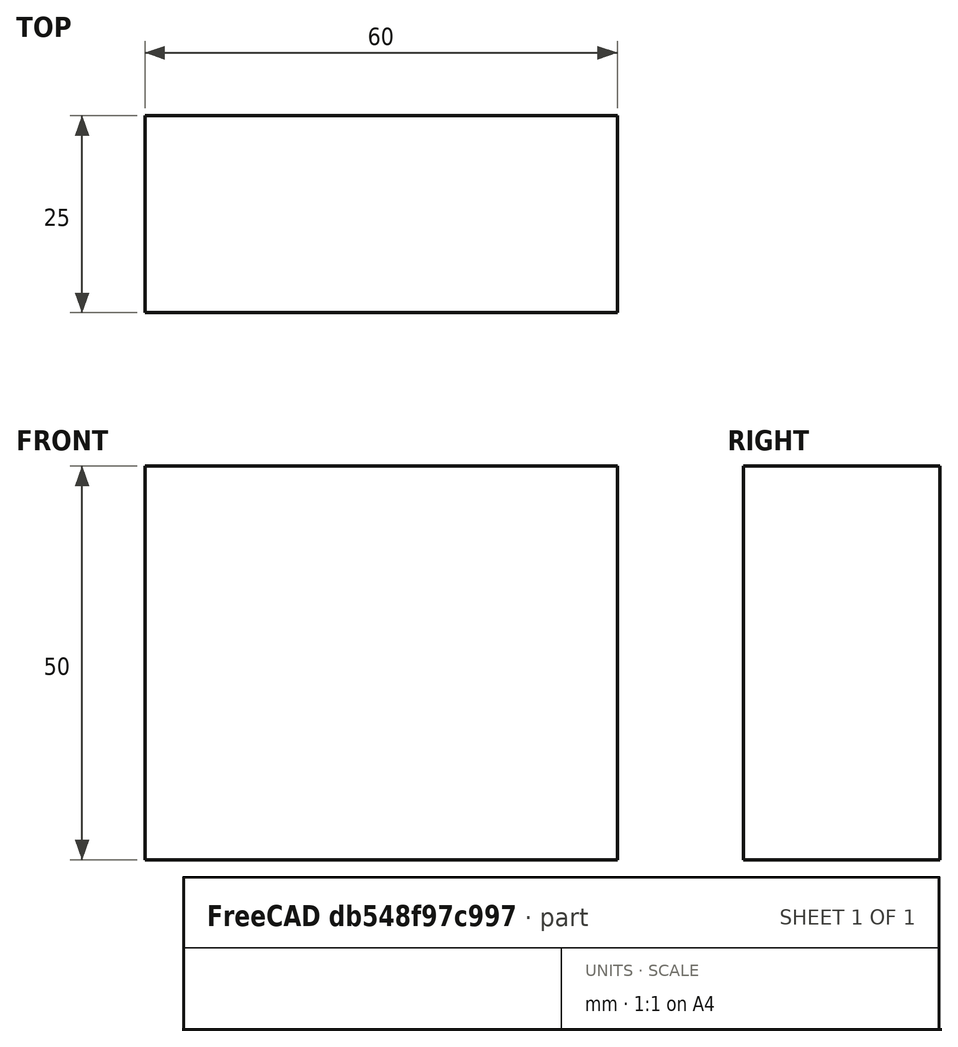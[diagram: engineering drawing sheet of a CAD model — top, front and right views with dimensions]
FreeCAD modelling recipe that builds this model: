
FCSTD DOCUMENT  (FreeCAD 0.15R4671 (Git))
Label: Flat Bar 60x25 EN10058 S235JR
License: All rights reserved
LicenseURL: http://en.wikipedia.org/wiki/All_rights_reserved
objects: Sketcher::SketchObject×1, Part::Extrusion×1
note: 2 computed .brp shape members not serialized (recipe doc carries the construction recipe); baked Part::Feature solids carry a one-line shape summary decoded from their .brp

FEATURE [Sketcher::SketchObject] Sketch
  sketch-geometry (4):
    g0: LineSegment StartX=-30 StartY=-12.5 StartZ=0 EndX=30 EndY=-12.5 EndZ=0
    g1: LineSegment StartX=30 StartY=-12.5 StartZ=0 EndX=30 EndY=12.5 EndZ=0
    g2: LineSegment StartX=30 StartY=12.5 StartZ=0 EndX=-30 EndY=12.5 EndZ=0
    g3: LineSegment StartX=-30 StartY=12.5 StartZ=0 EndX=-30 EndY=-12.5 EndZ=0
  constraints (12):
    c: Coincident(g0,g1)
    c: Coincident(g1,g2)
    c: Coincident(g2,g3)
    c: Coincident(g3,g0)
    c: Horizontal(g0)
    c: Horizontal(g2)
    c: Vertical(g1)
    c: Vertical(g3)
    c: Symmetric(g1,g2,g-2)
    c: Symmetric(g0,g1,g-1)
    c: DistanceY(g1) = 25
    c: DistanceX(g0) = 60
FEATURE [Part::Extrusion] Extrude  label="Flat Bar 60x25 EN10058 S235JR"
  Base = -> Sketch
  Dir = (0,0,50)
  Solid = true
